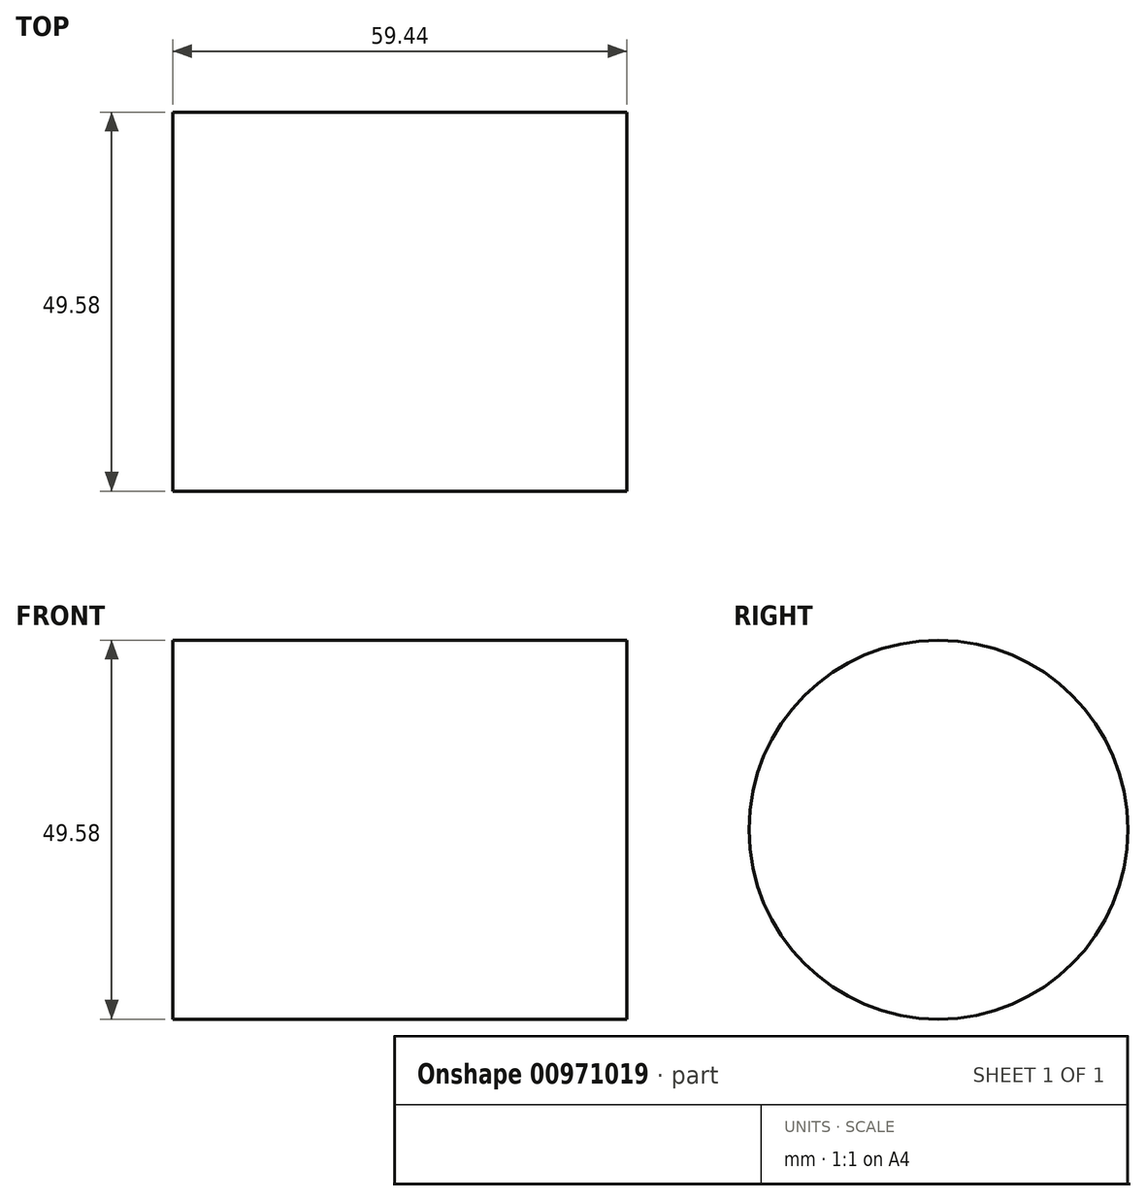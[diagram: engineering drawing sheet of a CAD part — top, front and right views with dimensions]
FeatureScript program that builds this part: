
annotation { "Feature Type Name" : "Feature", "Feature Type Description" : "" }
export const myFeature = defineFeature(function(context is Context, id is Id, definition is map)
    precondition{}
    {
        {
            var Q0;
            Q0=qCreatedBy(makeId("Right.planeOp"),FACE);
            var sketch = newSketch(context, id + "F0", { "sketchPlane" : qUnion([Q0])});
            skCircle(sketch, "E0", {"center": v(0, 0) * mm, "radius": 24.8 * mm});
            skSolve(sketch);
        }
        {
            var Q0;
            Q0 = qSketchRegion(id + "F0", true);
            extrude(context, id + "F1", {"entities" : qUnion([Q0]), "depth" : 59.44 * mm, "offsetDistance" : 25.4 * mm});
        }
    });
